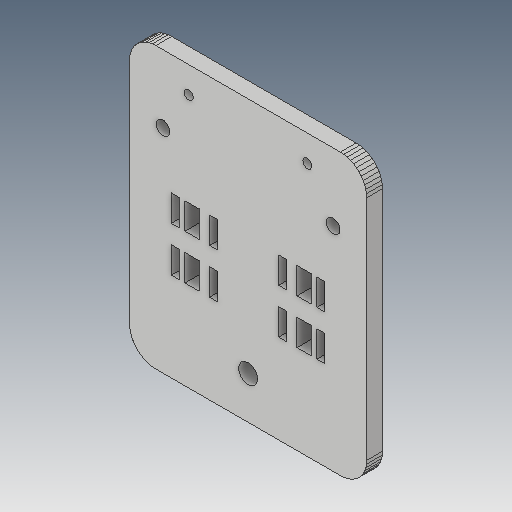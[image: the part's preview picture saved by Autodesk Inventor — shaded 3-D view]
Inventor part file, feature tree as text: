
AUTODESK INVENTOR PART (.ipt)
format: ipt  version: 2017 (Build 210142000, 142)  size: 312,320 bytes
history: native  units: mm
features: sketch x4, other x3
ambient origin geometry x8: Origin, YZ Plane, XZ Plane, XY Plane, X Axis, Y Axis, Z Axis, Center Point
bodies: Solid1 (feature_tree)
feature tree (7):
  other  "X-Axis-End-Plate_MIR.ipt"
  other  "Solid1::X-Axis-End-Plate_MIR.ipt"
  other  "TaggingFeature1"
  sketch  "Sketch1"  dims[d0=10.0mm]
  sketch  "Sketch2"
  sketch  "Sketch3"
  sketch  "Sketch4"
